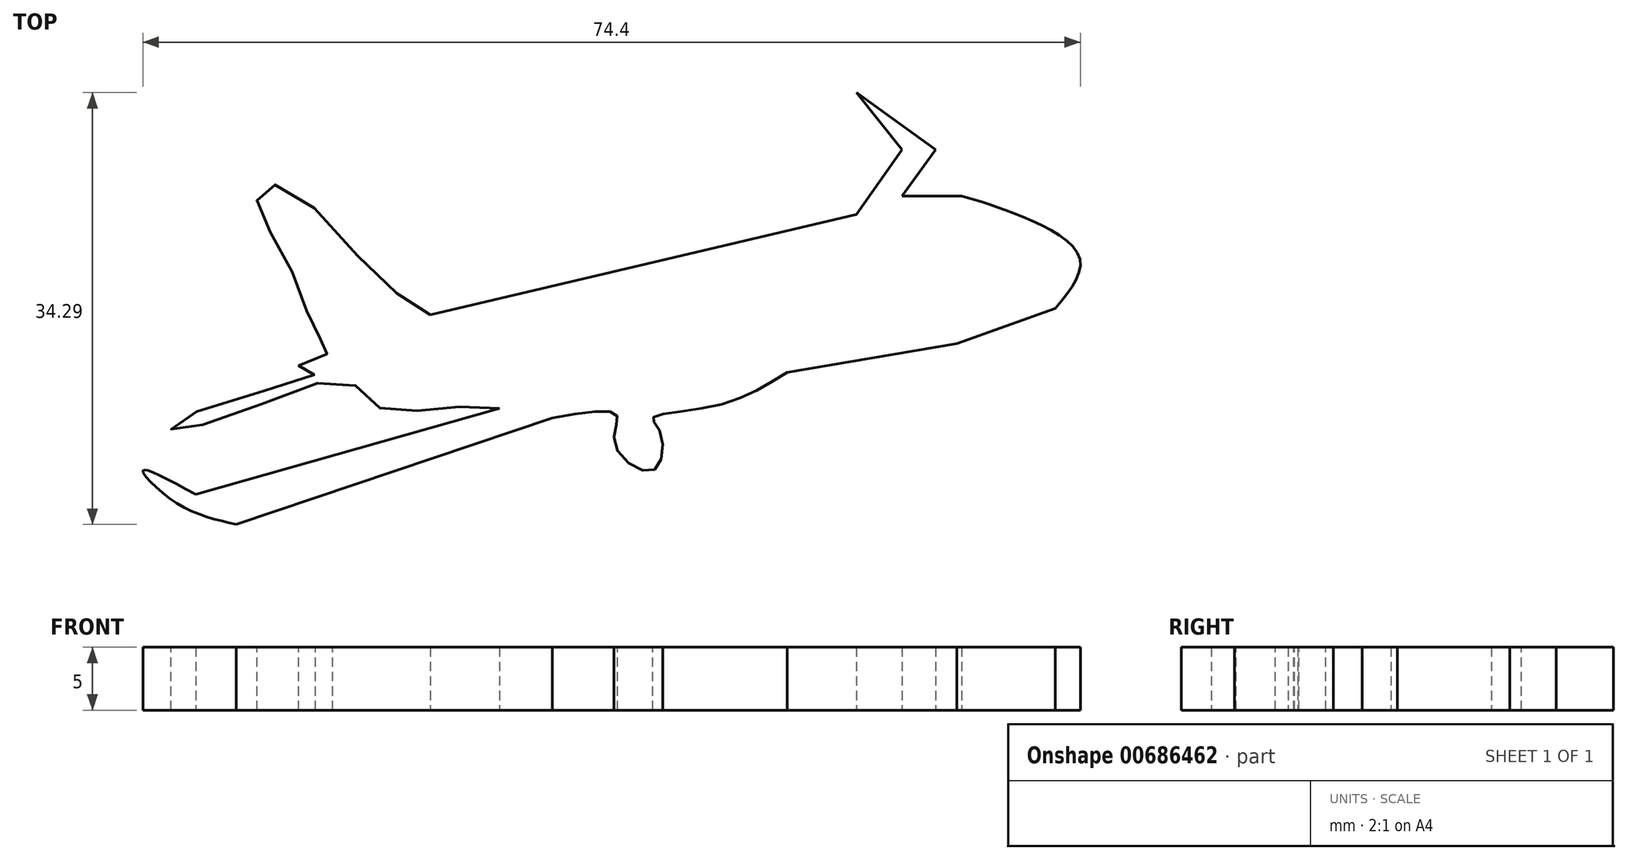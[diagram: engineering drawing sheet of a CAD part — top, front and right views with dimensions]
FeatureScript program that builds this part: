
annotation { "Feature Type Name" : "Feature", "Feature Type Description" : "" }
export const myFeature = defineFeature(function(context is Context, id is Id, definition is map)
    precondition{}
    {
        {
            var Q0;
            Q0=qCreatedBy(makeId("Top.planeOp"),FACE);
            var sketch = newSketch(context, id + "F0", { "sketchPlane" : qUnion([Q0])});
            skLineSegment(sketch, "E0.bottom", {"start": v(40, 25) * mm, "end": v(-40, 25) * mm});
            skLineSegment(sketch, "E0.top", {"start": v(40, -25) * mm, "end": v(-40, -25) * mm});
            skLineSegment(sketch, "E0.left", {"start": v(40, 25) * mm, "end": v(40, -25) * mm});
            skLineSegment(sketch, "E0.right", {"start": v(-40, 25) * mm, "end": v(-40, -25) * mm});
            skPoint(sketch, "E0.middle", {"position": v(0, 0) * mm});
            skSolve(sketch);
        }
        {
            var Q0;
            Q0=makeQuery(id+"F0.imprint","IMPRINT",FACE,{"disambiguationData":[TD([[makeQuery(id+"F0.imprint","IMPRINT",EDGE,{"derivedFrom":sQuery(id+"F0.wireOp",EDGE,"E0.bottom")}),1.0]])]});
            var sketch = newSketch(context, id + "F1", { "sketchPlane" : qUnion([Q0])});
            skLineSegment(sketch, "E1", {"start": v(-59.3, 23.94) * mm, "end": v(-25.49, 31.92) * mm});
            skLineSegment(sketch, "E2", {"start": v(-25.49, 31.92) * mm, "end": v(-21.88, 37.05) * mm});
            skLineSegment(sketch, "E3", {"start": v(-21.88, 37.05) * mm, "end": v(-25.49, 41.59) * mm});
            skLineSegment(sketch, "E4", {"start": v(-25.49, 41.59) * mm, "end": v(-19.22, 37.05) * mm});
            skLineSegment(sketch, "E5", {"start": v(-19.22, 37.05) * mm, "end": v(-21.88, 33.37) * mm});
            skLineSegment(sketch, "E6", {"start": v(-21.88, 33.37) * mm, "end": v(-17.13, 33.37) * mm});
            skPoint(sketch, "E7.3.internal.snap0", {"position": v(-7.78, 24.44) * mm});
            skFitSpline(sketch, "E7", {"points": [v(-17.13, 33.37) * mm, v(-12.76, 31.92) * mm, v(-7.78, 28.5) * mm, v(-9.72, 24.44) * mm], "startDerivative": vector(12.38, -3.59) * mm, "endDerivative": vector(-11.05, -13.42) * mm});
            skLineSegment(sketch, "E8", {"start": v(-9.72, 24.44) * mm, "end": v(-17.5, 21.66) * mm});
            skLineSegment(sketch, "E9", {"start": v(-17.5, 21.66) * mm, "end": v(-31, 19.38) * mm});
            skFitSpline(sketch, "E10", {"points": [v(-31, 19.38) * mm, v(-36.7, 16.72) * mm, v(-41.63, 15.77) * mm, v(-41.06, 14.63) * mm, v(-41.63, 11.59) * mm, v(-44.67, 13.68) * mm, v(-44.48, 15.96) * mm, v(-49.61, 15.77) * mm], "startDerivative": vector(-26.9, -16.97) * mm, "endDerivative": vector(-42.19, -7.37) * mm});
            skLineSegment(sketch, "E11", {"start": v(-49.61, 15.77) * mm, "end": v(-74.7, 7.3) * mm});
            skFitSpline(sketch, "E12", {"points": [v(-74.7, 7.3) * mm, v(-79.63, 9.12) * mm, v(-82.1, 11.59) * mm, v(-77.92, 9.69) * mm], "startDerivative": vector(-13.7, 3.09) * mm, "endDerivative": vector(17.78, -9.73) * mm});
            skLineSegment(sketch, "E13", {"start": v(-77.92, 9.69) * mm, "end": v(-53.8, 16.53) * mm});
            skFitSpline(sketch, "E14", {"points": [v(-53.8, 16.53) * mm, v(-58.73, 16.53) * mm, v(-63.3, 16.53) * mm, v(-65.76, 18.62) * mm, v(-73.55, 16.53) * mm, v(-79.82, 14.82) * mm, v(-77.16, 16.53) * mm, v(-68.42, 19.38) * mm, v(-69.75, 19.95) * mm, v(-67.1, 21.09) * mm, v(-68.23, 22.23) * mm, v(-69.37, 25.27) * mm, v(-72.03, 30.59) * mm, v(-72.98, 33.44) * mm, v(-71.08, 34.2) * mm, v(-63.86, 27.36) * mm, v(-59.3, 23.94) * mm], "startDerivative": vector(-72.56, 4.03) * mm, "endDerivative": vector(59.3, -34.96) * mm});
            skSolve(sketch);
        }
        {
            var Q0;
            Q0 = qSketchRegion(id + "F1", true);
            extrude(context, id + "F2", {"entities" : qUnion([Q0]), "depth" : 5 * mm, "offsetDistance" : 25 * mm});
        }
    });
